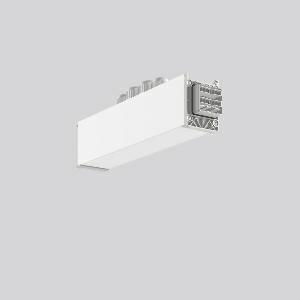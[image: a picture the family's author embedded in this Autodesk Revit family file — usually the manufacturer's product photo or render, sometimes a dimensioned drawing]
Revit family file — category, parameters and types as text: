
# Revit family: linedo_mitteleinspeisung_7pol_982698_002_3_561d
name_source: partatom
category: Lighting Fixtures
units: mm (PartAtom-declared; Revit-internal decimal feet)

## family parameters
Cut with Voids When Loaded = No
Host = Face
Light Source = No
Part Type = Normal
Room Calculation Point = No
Round Connector Dimension = Use Diameter
Shared = No

## types (1)
- LINEDO_Mitteleinspeisung_7pol
    Apparent Load = 0 VA
    Default Elevation = 1800 mm
    Description = Series: LINEDO
Middle power feed, 7-pole, connection socket / plug. Housing: extruded aluminium profile, powder-coated. Cover made of plastic, surface like housing. LINEDO plug system, plastic, light grey. 4 cable glands (2 x M20 and 2 x M25). Cable glands on top. Easy connection for rigid or flexible wires.
Colour: white
Length: 330 mm
Width: 58 mm
Height: 76 mm
Weight: 751 g
    Height = 76 mm
    Lamp = 0 x
    Length = 330 mm
    Luminous efficacy = 0 lm/W
    Manufacturer = RZB
    ModVariant = No
    Model = 982698.002.3
    Mounting Place = Ceiling
    Mounting Type = Surface mounted, Pendant
    Number of Poles = 1
    OnlyDefault = Yes
    Power Factor = 1
    Product Name = LINEDO_Mitteleinspeisung_7pol
    Product group = Surface mounted continuous line luminaire system
    ProductGroupID = 310
    Protection Class = Protection class I
    Protection Degree = IP 54
    RLX_Detail_Level = 1
    RLX_Emergency_Light_Flux = 0 lm
    RLX_Emergency_Type = 0
    RLX_Emergency_Type_DB = No
    RlxData = <blob elided: 20561 chars, md5=0bd3efd1>
    Standby Power = 0 W
    System Light Flux = 0 lm
    System Power = 0 W
    Type Comments = Product without accessories
    Type Image = 982698.002.jpg
    URL = http://relux.com
    VarID = ---
    Voltage = 0 V
    Weight = 0.00 kg
    Width = 58 mm

## geometry (parser evidence)
native form markers: Blend x4, Sweep x10
no freeform markers — native parametric forms only
